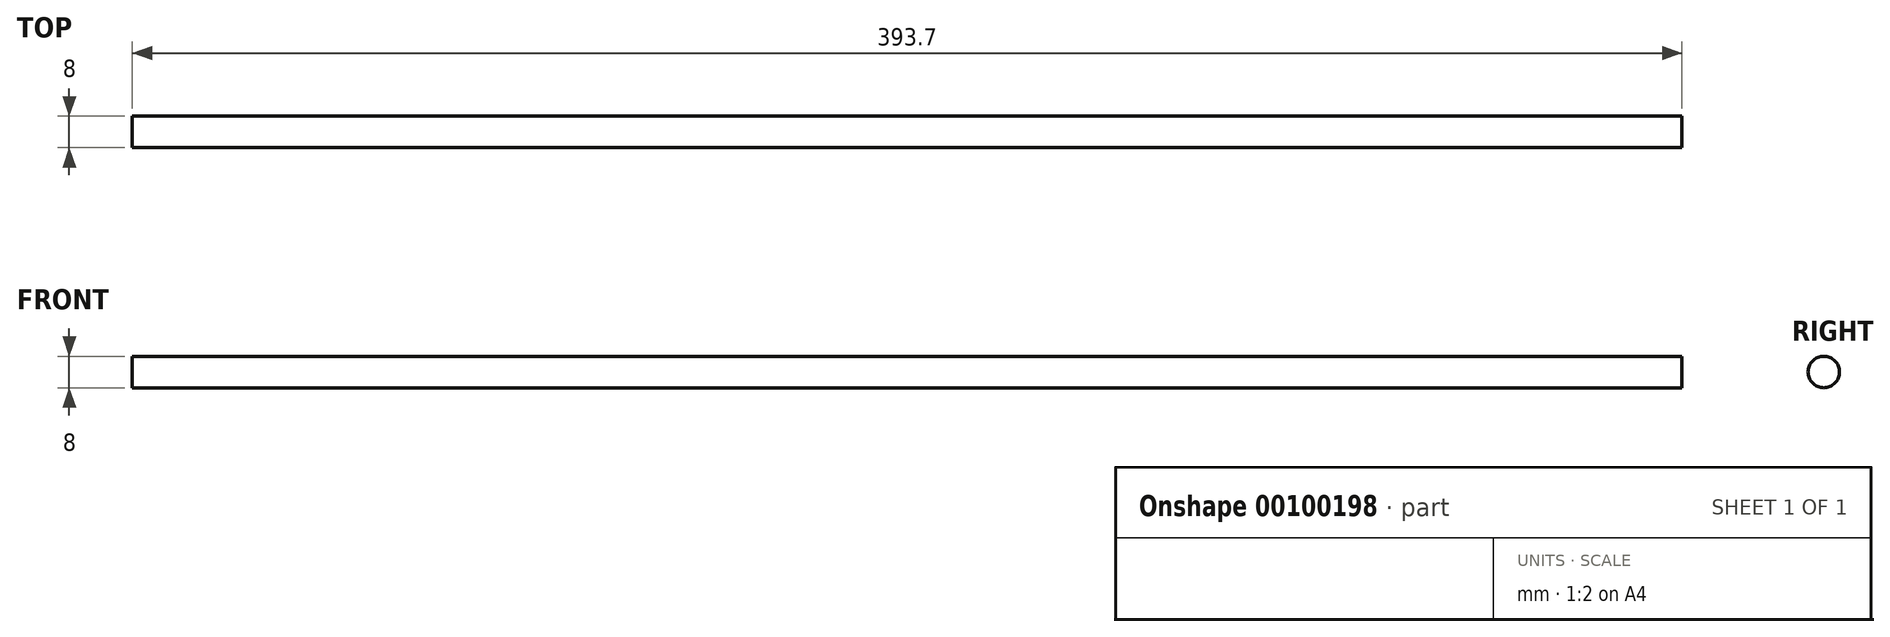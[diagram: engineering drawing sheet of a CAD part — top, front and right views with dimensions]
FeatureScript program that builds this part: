
annotation { "Feature Type Name" : "Feature", "Feature Type Description" : "" }
export const myFeature = defineFeature(function(context is Context, id is Id, definition is map)
    precondition{}
    {
        {
            var Q0;
            Q0=qCreatedBy(makeId("Right.planeOp"),FACE);
            var sketch = newSketch(context, id + "F0", { "sketchPlane" : qUnion([Q0])});
            skCircle(sketch, "E0", {"center": v(-12.83, 16.04) * mm, "radius": 4 * mm});
            skSolve(sketch);
        }
        {
            var Q0;
            Q0 = qSketchRegion(id + "F0", true);
            extrude(context, id + "F1", {"entities" : qUnion([Q0]), "depth" : 393.7 * mm});
        }
    });
